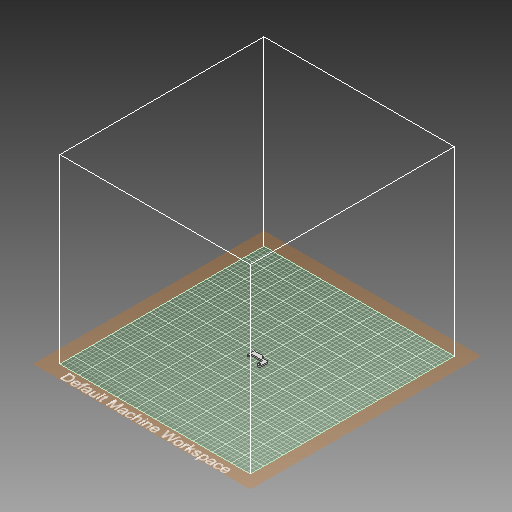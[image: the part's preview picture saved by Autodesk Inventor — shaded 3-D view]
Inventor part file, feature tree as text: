
AUTODESK INVENTOR PART (.ipt)
format: ipt  version: 2019 (Build 230136000, 136)  size: 273,408 bytes
history: native  units: mm
features: other x3, extrude x2, fillet x2, sketch x2, reference x1, projected_geometry x1
ambient origin geometry x8: Origin, YZ Plane, XZ Plane, XY Plane, X Axis, Y Axis, Z Axis, Center Point
bodies: Body1 (feature_tree)
feature tree (11):
  extrude  "Выдавливание2"  Depth=2.5mm
  extrude  "Выдавливание3"  Depth=3.0mm TaperAngle=0.0deg
  fillet  "Сопряжение3"  Radius=1.0mm
  fillet  "Сопряжение4"  Radius=2.0mm
  sketch  "Эскиз1"
  reference  "Ссылка1"
  sketch  "Эскиз2"
  projected_geometry  "Спроецированная петля1"
  other  "<userpath>\Documents\GitHub\Tesla_coil_V1\3dModels\TeslaCoil.iam"
  other  "TeslaCoil.iam"
  other  "TopBox:1"
